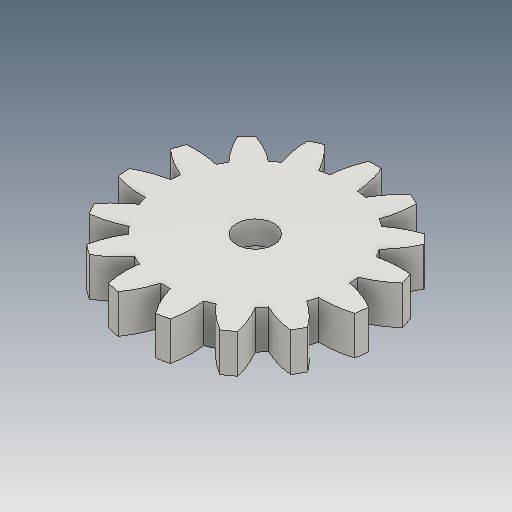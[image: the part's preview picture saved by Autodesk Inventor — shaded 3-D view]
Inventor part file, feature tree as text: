
AUTODESK INVENTOR PART (.ipt)
format: ipt  version: 2018 (Build 220112000, 112)  size: 226,816 bytes
history: native  units: mm
features: other x13, sketch x4, plane x4
ambient origin geometry x8: Origin, YZ Plane, XZ Plane, XY Plane, X Axis, Y Axis, Z Axis, Center Point
bodies: Volumenkörper1 (feature_tree)
feature tree (21):
  other  "Stirnzahnrad2"
  other  "Solid1::Stirnzahnrad2"
  other  "Bezeichnung1"
  sketch  "Sketch1"  dims[d0=10.0mm]
  sketch  "Sketch2"  dims[d16=40.0mm]
  sketch  "Skizze3"  dims[d17=0.0mm]
  sketch  "Skizze4"  dims[d41=0.0mm d43=40.0mm d46=40.0mm d47=0.0mm d48=0.0mm]
  plane  "XZ Plane_1"
  plane  "Work Plane2"
  plane  "Work Plane8"
  plane  "Work Plane9"
  other  "Z Axis_1"
  other  "Flä1"
  other  "Srf1::Abgeleitet"
  other  "Abstands-iMate"
  other  "Ausrichtungs-iMate"
  other  "Netz-iMate"
  other  "Achsen-iMate"
  other  "Positions-iMate"
  other  "Netz-iMate 2"
  other  "Startebenen-iMate"
